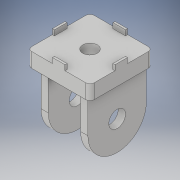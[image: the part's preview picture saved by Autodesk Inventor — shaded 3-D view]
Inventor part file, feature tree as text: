
AUTODESK INVENTOR PART (.ipt)
format: ipt  version: 2018 (Build 220112000, 112)  size: 202,240 bytes
history: native  units: mm
features: sketch x6, extrude x5, projected_geometry x2, hole x1
ambient origin geometry x8: Origin, YZ Plane, XZ Plane, XY Plane, X Axis, Y Axis, Z Axis, Center Point
bodies: Volumenkörper1 (feature_tree)
feature tree (14):
  extrude  "Extrusion1"  Depth=3.0mm
  extrude  "Extrusion2"  Depth=0.7mm
  extrude  "Extrusion3"  Depth=0.6mm
  extrude  "Extrusion4"  Depth=0.6mm
  extrude  "Extrusion5"  Depth=0.6mm
  hole  "Bohrung1"  [1 undecoded]
  sketch  "Skizze1"  dims[d0=3.0mm d1=3.0mm]
  sketch  "Skizze2"  dims[d2=0.2mm d3=0.7mm]
  projected_geometry  "Projizierte Kontur1"
  sketch  "Skizze3"  dims[d4=0.7mm d5=0.0mm d6=0.6mm]
  projected_geometry  "Projizierte Kontur2"
  sketch  "Skizze4"  dims[d7=0.1mm d8=0.6mm]
  sketch  "Skizze5"  dims[d9=0.6mm d10=0.6mm]
  sketch  "Skizze6"  dims[d11=0.1mm d12=0.1mm d13=0.1mm d14=0.25mm d15=0.0mm d16=0.35mm d17=0.35mm d18=2.8mm d19=0.2mm d20=0.55mm d21=1.55mm d22=0.0mm d23=0.35mm d24=0.0mm d25=0.35mm d26=0.0mm d27=0.8mm d28=6.0mm d29=4.0mm d30=2.0mm d31=90.0deg d32=8.0mm d33=20.594885mm]
note: 1 required parameter value undecoded (feature->parameter linkage not recoverable at this tier; creation-order binding heuristic only, values carry confidence <= 0.55)
